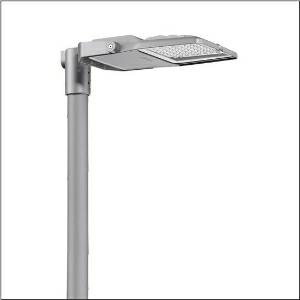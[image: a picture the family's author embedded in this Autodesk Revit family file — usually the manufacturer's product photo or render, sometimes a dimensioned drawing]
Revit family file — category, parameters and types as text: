
# Revit family: floodlight_fl_21_mini___pl61_5xa7776c4c3a_c7e0
name_source: partatom
category: Lighting Fixtures
units: mm (PartAtom-declared; Revit-internal decimal feet)

## family parameters
Cut with Voids When Loaded = No
Host = Face
Light Source = No
Part Type = Normal
Room Calculation Point = No
Round Connector Dimension = Use Diameter
Shared = No

## types (1)
- --- (1 x LED, 12460 lm, 89 W, 4000K)
    Apparent Load = 89 VA
    CIE Flux Codes = 33 65 98 100 100
    Color Rendering = 70
    Color Temperature = 4000K
    Default Elevation = 1800 mm
    Description = Floodlight FL 21 mini, floodlight, primary light control with lens, of PMMA, primary optical cover: protective disc, of toughened safety glass, transparent, light distribution: PL61, light emission: direct distribution, installation type: surface-mounted, LED, High Power LED, rated luminous flux: 12.460lm, luminous efficacy: 140lm/W, light colour: 740, colour temperature: 4000K, control gear: D4iSmart Interface (Zhaga), control: overheat protection, constant luminous flux control, time-dependent luminous flux control, flexible luminous flux parameterisation, pre-setting: logarithmic dimming characteristic, with terminal, 6-pole, mains connection: 220..240V, AC, 50/60Hz, start of lifetime: 89W, end of service life: 94W, reduction: 43W, mast bracket, of diecast aluminium, powder-coated, Siteco® metallic grey (DB 702S), corrosivity category C5 mid according to DIN EN ISO 12944, suitable for swimming pools, chlorine-resistant, sealing non-destructively replaceable, mast bracket, of steel, galvanised, powder-coated, Siteco® metallic grey (DB 702S), Smart Interface below and above, protection rating (complete): IP66, insulation class (complete): insulation class II (safety insulation), certification: CE, ENEC, VDE, protection symbol: D, impact resistance: IK08, permissible operating ambient temperature: -40..+40°C, permissible operating ambient temperature for outdoor applications: -40..+50°C, standard: DIN EN 12944, LABS conformity tested according to VDMA 24364:2018-05, packaging unit: 1 piece

Light Distribution: PL61
    Height = 70 mm
    Lamp = 1 x LED
    Lamp Light Flux = 12460 lm
    Lamp Power = 89 W
    Lamp count = 1
    Length = 485 mm
    Luminous efficacy = 140 lm/W
    Manufacturer = Siteco
    ModVariant = No
    Model = 5XA7776C4C3A
    Number of Poles = 1
    OnlyDefault = Yes
    Power Factor = 1
    Product Name = Floodlight FL 21 mini | PL61
    Product group = floodlight | pylon annexe
    ProductGroupID = 6200
    Protection Class = Protection class II
    Protection Degree = IP 66
    RLX_Detail_Level = 1
    RLX_Emergency_Light_Flux = 0 lm
    RLX_Emergency_Type = 0
    RLX_Emergency_Type_DB = No
    RlxData = <blob elided: 100893 chars, md5=ede04b47>
    Socket = socket
    Standby Power = 0 W
    System Light Flux = 12460 lm
    System Power = 89 W
    Type Comments = factory setting: luminous flux: 100 % | dim-lin: 254 | 456 mA
    Type Image = l_1007125.jpg
    URL = http://relux.com
    VarID = @adj_100548
    Voltage = 0 V
    Weight = 0.00 kg
    Width = 337 mm

## geometry (parser evidence)
native form markers: Blend x4, Sweep x14
no freeform markers — native parametric forms only
